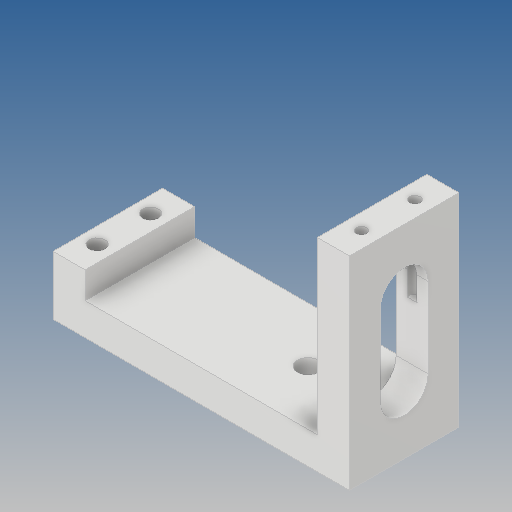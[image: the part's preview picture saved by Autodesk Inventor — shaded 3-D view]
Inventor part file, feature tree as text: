
AUTODESK INVENTOR PART (.ipt)
format: ipt  version: 2020 (Build 240168000, 168)  size: 159,232 bytes
history: native  units: mm
features: extrude x5, sketch x5, other x1
ambient origin geometry x8: Origin, YZ Plane, XZ Plane, XY Plane, X Axis, Y Axis, Z Axis, Center Point
bodies: Body1 (feature_tree)
feature tree (11):
  other  "Твердое тело1"
  extrude  "Выдавливание1"  Depth=38.0mm
  extrude  "Выдавливание2"  Depth=6.0mm
  extrude  "Выдавливание3"  Depth=6.0mm
  extrude  "Выдавливание4"  Depth=6.0mm
  extrude  "Выдавливание5"  Depth=11.0mm
  sketch  "Эскиз1"
  sketch  "Эскиз2"
  sketch  "Эскиз3"
  sketch  "Эскиз4"
  sketch  "Эскиз5"
